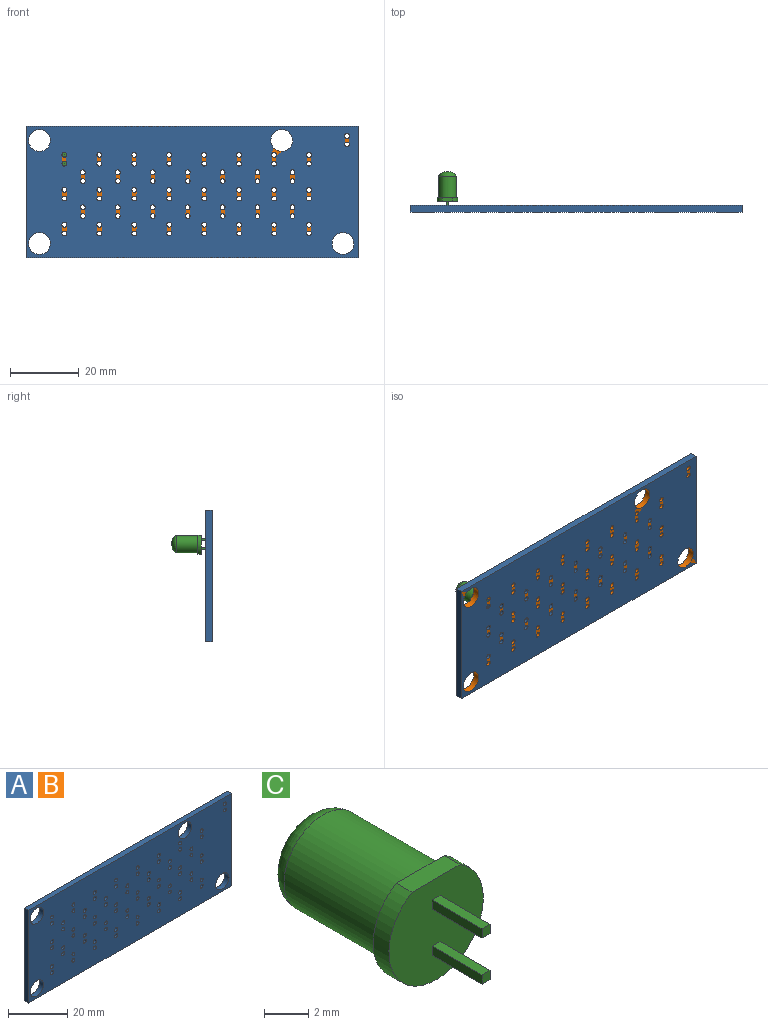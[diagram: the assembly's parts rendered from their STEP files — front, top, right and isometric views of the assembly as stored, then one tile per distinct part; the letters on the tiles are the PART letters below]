
ASSEMBLY  parts=3 mates=1
PART A: 88 faces, bbox 96.5x2x38.1 mm
  f0: plane 38.1x2mm, normal (1,0,0), area 76.2mm2, adj f1,f3,f4,f5
  f1: plane 96.52x2mm, normal (0,0,-1), area 193mm2, adj f0,f2,f4,f5
  f2: plane 38.1x2mm, normal (-1,0,0), area 76.2mm2, adj f1,f3,f4,f5
  f3: plane 96.52x2mm, normal (0,0,1), area 193mm2, adj f0,f2,f4,f5
  f4: plane 96.52x38.1mm, normal (0,1,0), area 3426.8mm2, adj f0,f1,f2,f3,f6,f7,f8,f9
  f5: plane 96.52x38.1mm, normal (0,-1,0), area 3426.8mm2, adj f0,f1,f2,f3,f6,f7,f8,f9
  f6: cylinder r=3.17mm len=6.35mm, axis (0,1,0), area 39.9mm2, adj f4,f5
  f7: cylinder r=3.17mm len=6.35mm, axis (0,1,0), area 39.9mm2, adj f4,f5
  f8: cylinder r=3.17mm len=6.35mm, axis (0,1,0), area 39.9mm2, adj f4,f5
  f9: cylinder r=3.17mm len=6.35mm, axis (0,1,0), area 39.9mm2, adj f4,f5
  f10: cylinder r=0.71mm len=2mm, axis (0,1,0), area 8.9mm2, adj f4,f5
  f11: cylinder r=0.71mm len=2mm, axis (0,1,0), area 8.9mm2, adj f4,f5
  f12: cylinder r=0.71mm len=2mm, axis (0,1,0), area 8.9mm2, adj f4,f5
  f13: cylinder r=0.71mm len=2mm, axis (0,1,0), area 8.9mm2, adj f4,f5
  f14: cylinder r=0.71mm len=2mm, axis (0,1,0), area 8.9mm2, adj f4,f5
  f15: cylinder r=0.71mm len=2mm, axis (0,1,0), area 8.9mm2, adj f4,f5
  f16: cylinder r=0.71mm len=2mm, axis (0,1,0), area 8.9mm2, adj f4,f5
  f17: cylinder r=0.71mm len=2mm, axis (0,1,0), area 8.9mm2, adj f4,f5
  f18: cylinder r=0.71mm len=2mm, axis (0,1,0), area 8.9mm2, adj f4,f5
  f19: cylinder r=0.71mm len=2mm, axis (0,1,0), area 8.9mm2, adj f4,f5
  f20: cylinder r=0.71mm len=2mm, axis (0,1,0), area 8.9mm2, adj f4,f5
  f21: cylinder r=0.71mm len=2mm, axis (0,1,0), area 8.9mm2, adj f4,f5
  f22: cylinder r=0.71mm len=2mm, axis (0,1,0), area 8.9mm2, adj f4,f5
  f23: cylinder r=0.71mm len=2mm, axis (0,1,0), area 8.9mm2, adj f4,f5
  f24: cylinder r=0.71mm len=2mm, axis (0,1,0), area 8.9mm2, adj f4,f5
  f25: cylinder r=0.71mm len=2mm, axis (0,1,0), area 8.9mm2, adj f4,f5
  f26: cylinder r=0.71mm len=2mm, axis (0,1,0), area 8.9mm2, adj f4,f5
  f27: cylinder r=0.71mm len=2mm, axis (0,1,0), area 8.9mm2, adj f4,f5
  f28: cylinder r=0.71mm len=2mm, axis (0,1,0), area 8.9mm2, adj f4,f5
  f29: cylinder r=0.71mm len=2mm, axis (0,1,0), area 8.9mm2, adj f4,f5
  f30: cylinder r=0.71mm len=2mm, axis (0,1,0), area 8.9mm2, adj f4,f5
  f31: cylinder r=0.71mm len=2mm, axis (0,1,0), area 8.9mm2, adj f4,f5
  f32: cylinder r=0.71mm len=2mm, axis (0,1,0), area 8.9mm2, adj f4,f5
  f33: cylinder r=0.71mm len=2mm, axis (0,1,0), area 8.9mm2, adj f4,f5
  f34: cylinder r=0.71mm len=2mm, axis (0,1,0), area 8.9mm2, adj f4,f5
  f35: cylinder r=0.71mm len=2mm, axis (0,1,0), area 8.9mm2, adj f4,f5
  f36: cylinder r=0.71mm len=2mm, axis (0,1,0), area 8.9mm2, adj f4,f5
  f37: cylinder r=0.71mm len=2mm, axis (0,1,0), area 8.9mm2, adj f4,f5
  f38: cylinder r=0.71mm len=2mm, axis (0,1,0), area 8.9mm2, adj f4,f5
  f39: cylinder r=0.71mm len=2mm, axis (0,1,0), area 8.9mm2, adj f4,f5
  f40: cylinder r=0.71mm len=2mm, axis (0,1,0), area 8.9mm2, adj f4,f5
  f41: cylinder r=0.71mm len=2mm, axis (0,1,0), area 8.9mm2, adj f4,f5
  f42: cylinder r=0.71mm len=2mm, axis (0,1,0), area 8.9mm2, adj f4,f5
  f43: cylinder r=0.71mm len=2mm, axis (0,1,0), area 8.9mm2, adj f4,f5
  f44: cylinder r=0.71mm len=2mm, axis (0,1,0), area 8.9mm2, adj f4,f5
  f45: cylinder r=0.71mm len=2mm, axis (0,1,0), area 8.9mm2, adj f4,f5
  f46: cylinder r=0.71mm len=2mm, axis (0,1,0), area 8.9mm2, adj f4,f5
  f47: cylinder r=0.71mm len=2mm, axis (0,1,0), area 8.9mm2, adj f4,f5
  f48: cylinder r=0.71mm len=2mm, axis (0,1,0), area 8.9mm2, adj f4,f5
  f49: cylinder r=0.71mm len=2mm, axis (0,1,0), area 8.9mm2, adj f4,f5
  f50: cylinder r=0.71mm len=2mm, axis (0,1,0), area 8.9mm2, adj f4,f5
  f51: cylinder r=0.71mm len=2mm, axis (0,1,0), area 8.9mm2, adj f4,f5
  f52: cylinder r=0.71mm len=2mm, axis (0,1,0), area 8.9mm2, adj f4,f5
  f53: cylinder r=0.71mm len=2mm, axis (0,1,0), area 8.9mm2, adj f4,f5
  f54: cylinder r=0.71mm len=2mm, axis (0,1,0), area 8.9mm2, adj f4,f5
  f55: cylinder r=0.71mm len=2mm, axis (0,1,0), area 8.9mm2, adj f4,f5
  f56: cylinder r=0.71mm len=2mm, axis (0,1,0), area 8.9mm2, adj f4,f5
  f57: cylinder r=0.71mm len=2mm, axis (0,1,0), area 8.9mm2, adj f4,f5
  f58: cylinder r=0.71mm len=2mm, axis (0,1,0), area 8.9mm2, adj f4,f5
  f59: cylinder r=0.71mm len=2mm, axis (0,1,0), area 8.9mm2, adj f4,f5
  f60: cylinder r=0.71mm len=2mm, axis (0,1,0), area 8.9mm2, adj f4,f5
  f61: cylinder r=0.71mm len=2mm, axis (0,1,0), area 8.9mm2, adj f4,f5
  f62: cylinder r=0.71mm len=2mm, axis (0,1,0), area 8.9mm2, adj f4,f5
  f63: cylinder r=0.71mm len=2mm, axis (0,1,0), area 8.9mm2, adj f4,f5
  f64: cylinder r=0.71mm len=2mm, axis (0,1,0), area 8.9mm2, adj f4,f5
  f65: cylinder r=0.71mm len=2mm, axis (0,1,0), area 8.9mm2, adj f4,f5
  f66: cylinder r=0.71mm len=2mm, axis (0,1,0), area 8.9mm2, adj f4,f5
  f67: cylinder r=0.71mm len=2mm, axis (0,1,0), area 8.9mm2, adj f4,f5
  f68: cylinder r=0.71mm len=2mm, axis (0,1,0), area 8.9mm2, adj f4,f5
  f69: cylinder r=0.71mm len=2mm, axis (0,1,0), area 8.9mm2, adj f4,f5
  f70: cylinder r=0.71mm len=2mm, axis (0,1,0), area 8.9mm2, adj f4,f5
  f71: cylinder r=0.71mm len=2mm, axis (0,1,0), area 8.9mm2, adj f4,f5
  f72: cylinder r=0.71mm len=2mm, axis (0,1,0), area 8.9mm2, adj f4,f5
  f73: cylinder r=0.71mm len=2mm, axis (0,1,0), area 8.9mm2, adj f4,f5
  f74: cylinder r=0.71mm len=2mm, axis (0,1,0), area 8.9mm2, adj f4,f5
  f75: cylinder r=0.71mm len=2mm, axis (0,1,0), area 8.9mm2, adj f4,f5
  f76: cylinder r=0.71mm len=2mm, axis (0,1,0), area 8.9mm2, adj f4,f5
  f77: cylinder r=0.71mm len=2mm, axis (0,1,0), area 8.9mm2, adj f4,f5
  f78: cylinder r=0.71mm len=2mm, axis (0,1,0), area 8.9mm2, adj f4,f5
  f79: cylinder r=0.71mm len=2mm, axis (0,1,0), area 8.9mm2, adj f4,f5
  f80: cylinder r=0.71mm len=2mm, axis (0,1,0), area 8.9mm2, adj f4,f5
  f81: cylinder r=0.71mm len=2mm, axis (0,1,0), area 8.9mm2, adj f4,f5
  f82: cylinder r=0.71mm len=2mm, axis (0,1,0), area 8.9mm2, adj f4,f5
  f83: cylinder r=0.71mm len=2mm, axis (0,1,0), area 8.9mm2, adj f4,f5
  f84: cylinder r=0.71mm len=2mm, axis (0,1,0), area 8.9mm2, adj f4,f5
  f85: cylinder r=0.71mm len=2mm, axis (0,1,0), area 8.9mm2, adj f4,f5
  f86: cylinder r=0.71mm len=2mm, axis (0,1,0), area 8.9mm2, adj f4,f5
  f87: cylinder r=0.71mm len=2mm, axis (0,1,0), area 8.9mm2, adj f4,f5
PART B: same geometry as A
PART C: 16 faces, bbox 6x10.3x5.6 mm
  f0: plane 3.18x0.51mm, normal (1,0,0), area 1.6mm2, adj f1,f3,f8,f15
  f1: plane 3.18x0.51mm, normal (0,0,1), area 1.6mm2, adj f0,f2,f8,f15
  f2: plane 3.18x0.51mm, normal (-1,0,0), area 1.6mm2, adj f1,f3,f8,f15
  f3: plane 3.18x0.51mm, normal (0,0,-1), area 1.6mm2, adj f0,f2,f8,f15
  f4: plane 3.18x0.51mm, normal (1,0,0), area 1.6mm2, adj f5,f7,f8,f14
  f5: plane 3.18x0.51mm, normal (0,0,1), area 1.6mm2, adj f4,f6,f8,f14
  f6: plane 3.18x0.51mm, normal (-1,0,0), area 1.6mm2, adj f5,f7,f8,f14
  f7: plane 3.18x0.51mm, normal (0,0,-1), area 1.6mm2, adj f4,f6,f8,f14
  f8: plane 6x5.58mm, normal (0,-1,0), area 26.9mm2, adj f0,f1,f2,f3,f4,f5,f6,f7
  f9: cylinder r=3mm len=6mm, axis (0,-1,0), area 15.7mm2, adj f8,f10,f11
  f10: plane 3.05x1mm, normal (0,0,1), area 3mm2, adj f8,f9,f11
  f11: plane 6x5.58mm, normal (0,1,0), area 7.8mm2, adj f9,f10,f12
  f12: cylinder r=2.5mm len=6.17mm, axis (0,-1,0), area 97mm2, adj f11,f13
  f13: revolved ~5x2.5mm, area 0mm2, adj f12
  f14: plane 0.51x0.51mm, normal (0,-1,0), area 0.3mm2, adj f4,f5,f6,f7
  f15: plane 0.51x0.51mm, normal (0,-1,0), area 0.3mm2, adj f0,f1,f2,f3
PLACE A t=(20.51,22.86,16.53)mm
PLACE B t=(20.51,22.86,16.53)mm
PLACE C t=(-16.84,26.04,25.8)mm
MATE fastened C.f15 <-> A.f55  axis (0,1,0) through (-16.59,22.86,27.32)mm
